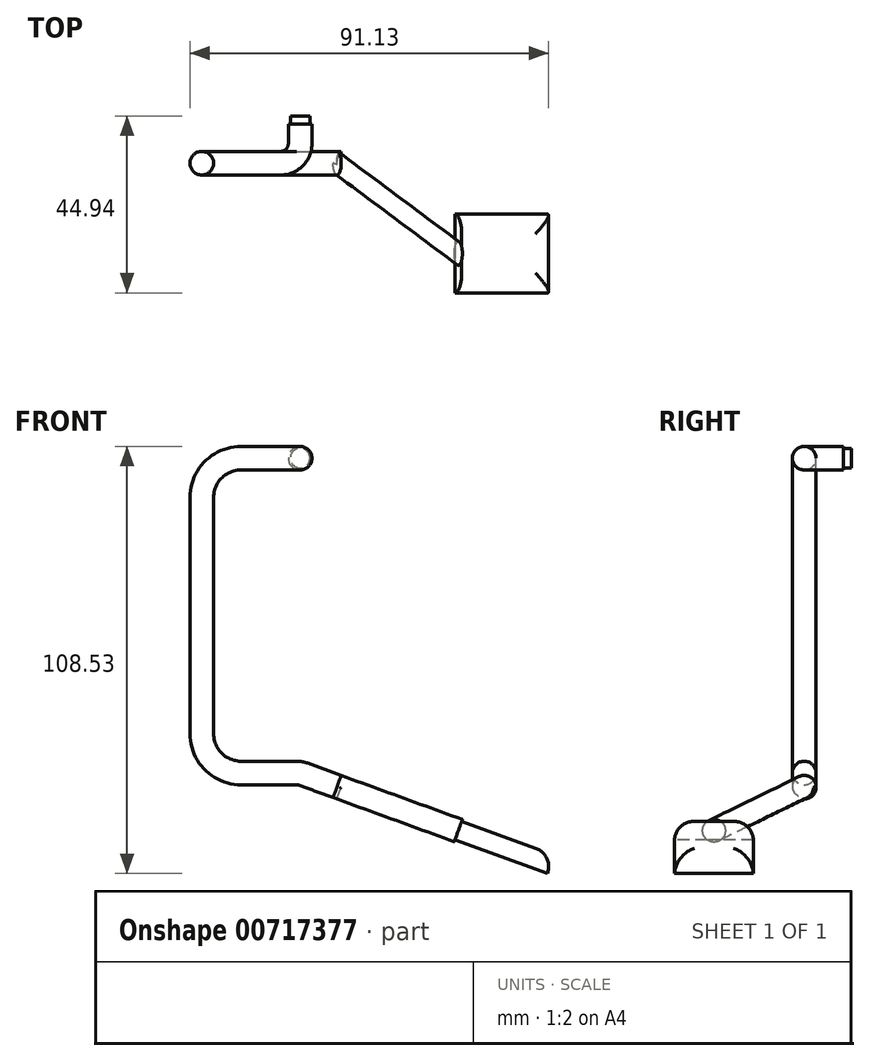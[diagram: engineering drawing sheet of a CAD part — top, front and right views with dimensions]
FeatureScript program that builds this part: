
annotation { "Feature Type Name" : "Feature", "Feature Type Description" : "" }
export const myFeature = defineFeature(function(context is Context, id is Id, definition is map)
    precondition{}
    {
        {
            var Q0;
            Q0=qCreatedBy(makeId("Front.planeOp"),FACE);
            var sketch = newSketch(context, id + "F0", { "sketchPlane" : qUnion([Q0])});
            skCircle(sketch, "E0", {"center": v(0, 0) * mm, "radius": 2.5 * mm});
            skSolve(sketch);
        }
        {
            var Q0;
            Q0=makeQuery(id+"F0.imprint","IMPRINT",FACE,{"disambiguationData":[TD([[makeQuery(id+"F0.imprint","IMPRINT",EDGE,{"derivedFrom":sQuery(id+"F0.wireOp",EDGE,"E0")}),1.0]])]});
            extrude(context, id + "F1", {"entities" : qUnion([Q0]), "depth" : 2 * mm, "offsetDistance" : 25 * mm});
        }
        {
            var Q0;
            Q0=makeQuery(id+"F1.opExtrude","CAP_FACE",FACE,{"disambiguationData":[OSD([sQuery(id+"F0.wireOp",EDGE,"E0")])],"isStart":false});
            var sketch = newSketch(context, id + "F2", { "sketchPlane" : qUnion([Q0])});
            skCircle(sketch, "E1", {"center": v(0, 0) * mm, "radius": 3 * mm});
            skSolve(sketch);
        }
        {
            var Q0;
            Q0=qCreatedBy(makeId("Top.planeOp"),FACE);
            var sketch = newSketch(context, id + "F3", { "sketchPlane" : qUnion([Q0])});
            skLineSegment(sketch, "E2.0", {"start": v(3, -2) * mm, "end": v(-3, -2) * mm, "construction": true});
            skLineSegment(sketch, "E3", {"start": v(0, -2) * mm, "end": v(0, -7) * mm});
            skLineSegment(sketch, "E4", {"start": v(-5, -12) * mm, "end": v(-10, -12) * mm});
            skPoint(sketch, "E5.visualSharp", {"position": v(0, -12) * mm});
            skArc(sketch, "E5.filletArc", {"start": v(-5, -12) * mm, "mid": v(-1.46, -10.54) * mm, "end": v(0, -7) * mm});
            skSolve(sketch);
        }
        {
            var Q0;
            Q0 = qSketchRegion(id + "F2", true);
            var Q1;
            Q1 = qConstructionFilter(qBodyType(qCreatedBy(id + "F3" ,EDGE), BodyType.WIRE), ConstructionObject.NO);
            sweep(context, id + "F4", {"operationType" : NewBodyOperationType.ADD, "profiles" : qUnion([Q0]), "path" : qUnion([Q1])});
        }
        {
            var Q0;
            Q0=makeQuery(id+"F4.opSweep","CAP_FACE",FACE,{"disambiguationData":[OSD([sQuery(id+"F2.wireOp",EDGE,"E1"),sQuery(id+"F3.wireOp",VERTEX,"E4.end")])],"isStart":false});
            var sketch = newSketch(context, id + "F5", { "sketchPlane" : qUnion([Q0])});
            skCircle(sketch, "E6.0.0", {"center": v(12, 0) * mm, "radius": 3 * mm});
            skSolve(sketch);
        }
        {
            var Q0;
            Q0=qCreatedBy(makeId("Front.planeOp"),FACE);
            cPlane(context, id + "F6", {"entities" : qUnion([Q0]), "cplaneType" : CPlaneType.OFFSET, "offset" : 12 * mm, "width" : 150 * mm, "height" : 150 * mm});
        }
        {
            var Q0;
            Q0=qCreatedBy(id+"F6.planeOp",FACE);
            var sketch = newSketch(context, id + "F7", { "sketchPlane" : qUnion([Q0])});
            skLineSegment(sketch, "E7", {"start": v(-10, 0) * mm, "end": v(-15, 0) * mm});
            skLineSegment(sketch, "E8", {"start": v(-25, -10) * mm, "end": v(-25, -70) * mm});
            skLineSegment(sketch, "E9", {"start": v(-15, -80) * mm, "end": v(-0.88, -80) * mm});
            skLineSegment(sketch, "E10", {"start": v(0.83, -80.3) * mm, "end": v(9.4, -83.42) * mm});
            skLineSegment(sketch, "E11.0", {"start": v(-10, -3) * mm, "end": v(-10, 3) * mm, "construction": true});
            skPoint(sketch, "E12.visualSharp", {"position": v(-25, 0) * mm});
            skArc(sketch, "E12.filletArc", {"start": v(-15, 0) * mm, "mid": v(-22.07, -2.93) * mm, "end": v(-25, -10) * mm});
            skPoint(sketch, "E13.visualSharp", {"position": v(-25, -80) * mm});
            skArc(sketch, "E13.filletArc", {"start": v(-25, -70) * mm, "mid": v(-22.07, -77.07) * mm, "end": v(-15, -80) * mm});
            skPoint(sketch, "E14.visualSharp", {"position": v(0, -80) * mm});
            skArc(sketch, "E14.filletArc", {"start": v(0.83, -80.3) * mm, "mid": v(-0.01, -80.08) * mm, "end": v(-0.88, -80) * mm});
            skSolve(sketch);
        }
        {
            var Q0;
            Q0=makeQuery(id+"F5.imprint","IMPRINT",FACE,{"disambiguationData":[TD([[makeQuery(id+"F5.imprint","IMPRINT",EDGE,{"derivedFrom":sQuery(id+"F5.wireOp",EDGE,"E6.0.0")}),1.0]])]});
            var Q1;
            Q1 = qConstructionFilter(qBodyType(qCreatedBy(id + "F7" ,EDGE), BodyType.WIRE), ConstructionObject.NO);
            sweep(context, id + "F8", {"operationType" : NewBodyOperationType.ADD, "profiles" : qUnion([Q0]), "path" : qUnion([Q1])});
        }
        {
            var Q0;
            Q0=makeQuery(id+"F8.opSweep","CAP_FACE",FACE,{"disambiguationData":[OSD([sQuery(id+"F5.wireOp",EDGE,"E6.0.0"),sQuery(id+"F7.wireOp",VERTEX,"E10.end")])],"isStart":false});
            var sketch = newSketch(context, id + "F9", { "sketchPlane" : qUnion([Q0])});
            skArc(sketch, "E15.0.0", {"start": v(-15, -75.18) * mm, "mid": v(-12, -78.18) * mm, "end": v(-9, -75.18) * mm});
            skLineSegment(sketch, "E16", {"start": v(-15, -75.18) * mm, "end": v(-9, -75.18) * mm});
            skSolve(sketch);
        }
        {
            var Q0;
            Q0=makeQuery(id+"F9.imprint","IMPRINT",FACE,{"disambiguationData":[TD([[makeQuery(id+"F9.imprint","IMPRINT",EDGE,{"derivedFrom":sQuery(id+"F9.wireOp",EDGE,"E15.0.0")}),1.0]])]});
            extrude(context, id + "F10", {"entities" : qUnion([Q0]), "operationType" : NewBodyOperationType.ADD, "depth" : 1 * mm, "offsetDistance" : 25 * mm});
        }
        {
            var Q0;
            Q0=makeQuery(id+"F10.opExtrude","SWEPT_FACE",FACE,{"disambiguationData":[OSD([sQuery(id+"F9.wireOp",EDGE,"E16")])]});
            var sketch = newSketch(context, id + "F11", { "sketchPlane" : qUnion([Q0])});
            skLineSegment(sketch, "E17", {"start": v(37.36, -12) * mm, "end": v(70.13, -34.94) * mm});
            skLineSegment(sketch, "E18", {"start": v(37.36, -12) * mm, "end": v(16.84, -12) * mm, "construction": true});
            skSolve(sketch);
        }
        {
            var Q0;
            Q0 = qSketchRegion(id + "F9", true);
            var Q1;
            Q1=makeQuery(id+"F8.opSweep","CAP_FACE",FACE,{"disambiguationData":[OSD([sQuery(id+"F5.wireOp",EDGE,"E6.0.0"),sQuery(id+"F7.wireOp",VERTEX,"E10.end")])],"isStart":false});
            var Q2;
            Q2 = qConstructionFilter(qBodyType(qCreatedBy(id + "F11" ,EDGE), BodyType.WIRE), ConstructionObject.NO);
            sweep(context, id + "F12", {"operationType" : NewBodyOperationType.ADD, "profiles" : qUnion([Q0, Q1]), "path" : qUnion([Q2])});
        }
        {
            var Q0;
            {var subQ0=sQuery(id+"F11.wireOp",VERTEX,"E17.end");Q0=makeQuery(id+"F12.boolean.opBoolean","MERGE",FACE,{"derivedFrom":[makeQuery(id+"F12.opSweep","CAP_FACE",FACE,{"disambiguationData":[OSD([sQuery(id+"F9.wireOp",EDGE,"E15.0.0"),sQuery(id+"F9.wireOp",EDGE,"E16"),subQ0])],"isStart":false}),makeQuery(id+"F12.opSweep","CAP_FACE",FACE,{"disambiguationData":[OSD([sQuery(id+"F5.wireOp",EDGE,"E6.0.0"),sQuery(id+"F7.wireOp",VERTEX,"E10.end"),subQ0])],"isStart":false})]});}
            var sketch = newSketch(context, id + "F13", { "sketchPlane" : qUnion([Q0])});
            skLineSegment(sketch, "E19.bottom", {"start": v(-24.94, -77.68) * mm, "end": v(-44.94, -77.68) * mm});
            skLineSegment(sketch, "E19.top", {"start": v(-24.94, -72.68) * mm, "end": v(-44.94, -72.68) * mm});
            skLineSegment(sketch, "E19.left", {"start": v(-24.94, -77.68) * mm, "end": v(-24.94, -72.68) * mm});
            skLineSegment(sketch, "E19.right", {"start": v(-44.94, -77.68) * mm, "end": v(-44.94, -72.68) * mm});
            skPoint(sketch, "E19.middle", {"position": v(-34.94, -75.18) * mm});
            skSolve(sketch);
        }
        {
            var Q0;
            Q0 = qSketchRegion(id + "F13", true);
            extrude(context, id + "F14", {"entities" : qUnion([Q0]), "operationType" : NewBodyOperationType.ADD, "depth" : 25 * mm, "offsetDistance" : 25 * mm});
        }
        {
            var Q0;
            Q0=makeQuery(id+"F14.opExtrude","SWEPT_EDGE",EDGE,{"disambiguationData":[OSD([sQuery(id+"F13.wireOp",EDGE,"E19.top"),sQuery(id+"F13.wireOp",EDGE,"E19.right")])]});
            var Q1;
            Q1=makeQuery(id+"F14.opExtrude","CAP_EDGE",EDGE,{"disambiguationData":[OSD([sQuery(id+"F13.wireOp",EDGE,"E19.top")])],"isStart":false});
            var Q2;
            Q2=makeQuery(id+"F14.opExtrude","SWEPT_EDGE",EDGE,{"disambiguationData":[OSD([sQuery(id+"F13.wireOp",EDGE,"E19.top"),sQuery(id+"F13.wireOp",EDGE,"E19.left")])]});
            fillet(context, id + "F15", {"entities" : qUnion([Q0, Q1, Q2]), "radius" : 5 * mm, "tangentPropagation" : true, "allowEdgeOverflow" : false});
        }
    });
